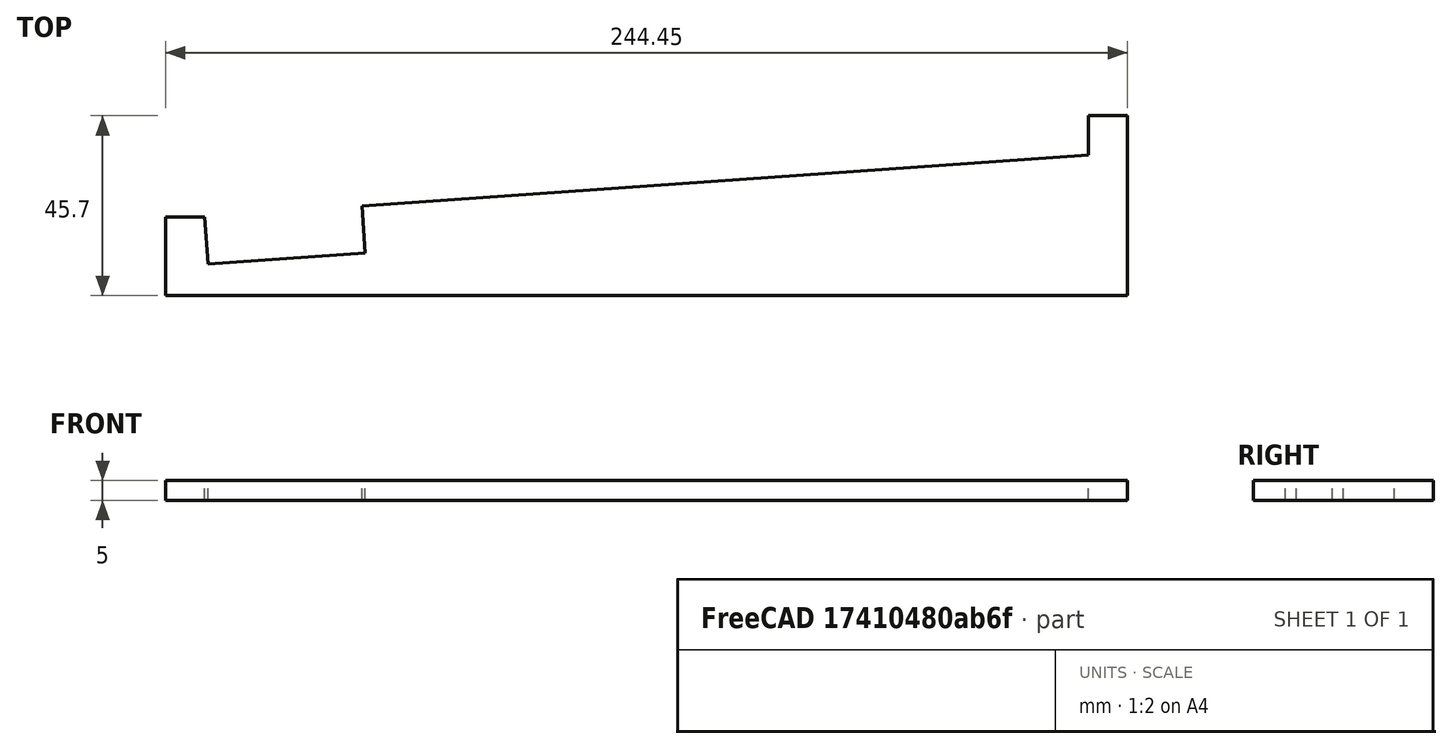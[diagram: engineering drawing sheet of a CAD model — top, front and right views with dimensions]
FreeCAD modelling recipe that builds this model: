
FCSTD DOCUMENT  (FreeCAD 1.0R39319 (Git))
Label: Ikea265_10_6l_laserstand
License: All rights reserved
LicenseURL: https://en.wikipedia.org/wiki/All_rights_reserved
objects: Sketcher::SketchObject×2, PartDesign::Pad×1, PartDesign::Body×1
note: 8 computed .brp shape members not serialized (recipe doc carries the construction recipe); baked Part::Feature solids carry a one-line shape summary decoded from their .brp

FEATURE [Sketcher::SketchObject] Sketch
  ArcFitTolerance = 1e-06
  AttachmentSupport = -> [XY_Plane]
  FullyConstrained = true
  MakeInternals = false
  MapMode = 5
  sketch-geometry (11):
    g0: LineSegment StartX=49.9026 StartY=22.7903 StartZ=0 EndX=234.452 EndY=35.6952 EndZ=0
    g1: LineSegment StartX=234.452 StartY=35.6952 StartZ=0 EndX=234.452 EndY=45.6952 EndZ=0
    g2: LineSegment StartX=0 StartY=0 StartZ=0 EndX=244.452 EndY=0 EndZ=0
    g3: LineSegment StartX=244.452 StartY=0 StartZ=0 EndX=244.452 EndY=45.6952 EndZ=0
    g4: LineSegment StartX=234.452 StartY=45.6952 StartZ=0 EndX=244.452 EndY=45.6952 EndZ=0
    g5: LineSegment StartX=0 StartY=0 StartZ=0 EndX=0 EndY=20 EndZ=0
    g6: LineSegment StartX=0 StartY=20 StartZ=0 EndX=10 EndY=20 EndZ=0
    g7: LineSegment StartX=10 StartY=20 StartZ=0 EndX=10.8371 EndY=8.02923 EndZ=0
    g8: LineSegment StartX=10.8371 StartY=8.02923 StartZ=0 EndX=50.7396 EndY=10.8195 EndZ=0
    g9: LineSegment StartX=49.9026 StartY=22.7903 StartZ=0 EndX=50.7396 EndY=10.8195 EndZ=0
    g10: LineSegment [constr] StartX=49.9026 StartY=22.7903 StartZ=0 EndX=10 EndY=20 EndZ=0
  constraints (31):
    c: Coincident(g1,g0)
    c: Angle(g1,g0) = 1.64061
    c: PointOnObject(g2,g-1)
    c: Coincident(g3,g2)
    c: Vertical(g3)
    c: Coincident(g4,g1)
    c: Coincident(g4,g3)
    c: Horizontal(g4)
    c: Coincident(g5,g2)
    c: Vertical(g5)
    c: Coincident(g6,g5)
    c: Horizontal(g6)
    c: Coincident(g7,g6)
    c: Coincident(g8,g7)
    c: Coincident(g9,g0)
    c: Coincident(g9,g8)
    c: Parallel(g8,g0)
    c: Perpendicular(g9,g0)
    c: Coincident(g10,g0)
    c: Parallel(g10,g0)
    c: Angle(g0,g5) = 1.50098
    c: Distance(g7,g8) = 40
    c: Distance(g9) = 12
    c: Coincident(g10,g6)
    c: Perpendicular(g8,g7)
    c: Distance(g6,g0) = 225
    c: DistanceX(g4,g4) = 10
    c: DistanceY(g1,g1) = 10
    c: DistanceX(g6,g6) = 10
    c: DistanceY(g5,g5) = 20
    c: Coincident(g-1,g2)
FEATURE [PartDesign::Pad] Pad
  Direction = (0,0,1)
  Length = 5
  Length2 = 10
  Midplane = true
  Profile = -> Sketch
  ReferenceAxis = -> Sketch [N_Axis]
  Refine = true
  Suppressed = false
  Type = 0
FEATURE [Sketcher::SketchObject] Sketch001
  ArcFitTolerance = 1e-06
  AttachmentSupport = -> [YZ_Plane]
  FullyConstrained = true
  MakeInternals = false
  MapMode = 5
  Placement = pos=(0,0,0) rot=(0.57735,0.57735,0.57735;2.0944rad)
  sketch-geometry (5):
    g0: LineSegment StartX=-1 StartY=-12.5 StartZ=0 EndX=1 EndY=-12.5 EndZ=0
    g1: LineSegment StartX=1 StartY=-12.5 StartZ=0 EndX=1 EndY=12.5 EndZ=0
    g2: LineSegment StartX=1 StartY=12.5 StartZ=0 EndX=-1 EndY=12.5 EndZ=0
    g3: LineSegment StartX=-1 StartY=12.5 StartZ=0 EndX=-1 EndY=-12.5 EndZ=0
    g4: GeomPoint [constr] X=0 Y=0 Z=0
  constraints (12):
    c: Coincident(g0,g1)
    c: Coincident(g1,g2)
    c: Coincident(g2,g3)
    c: Coincident(g3,g0)
    c: Horizontal(g0)
    c: Horizontal(g2)
    c: Vertical(g1)
    c: Vertical(g3)
    c: Symmetric(g2,g0,g4)
    c: Distance(g1,g3) = 2
    c: Coincident(g-1,g4)
    c: DistanceY(g3,g3) = 25
FEATURE [PartDesign::Body] Body
  AllowCompound = false
  Group = -> [Sketch,Pad,Sketch001]
  Origin = -> Origin
  Tip = -> Pad
